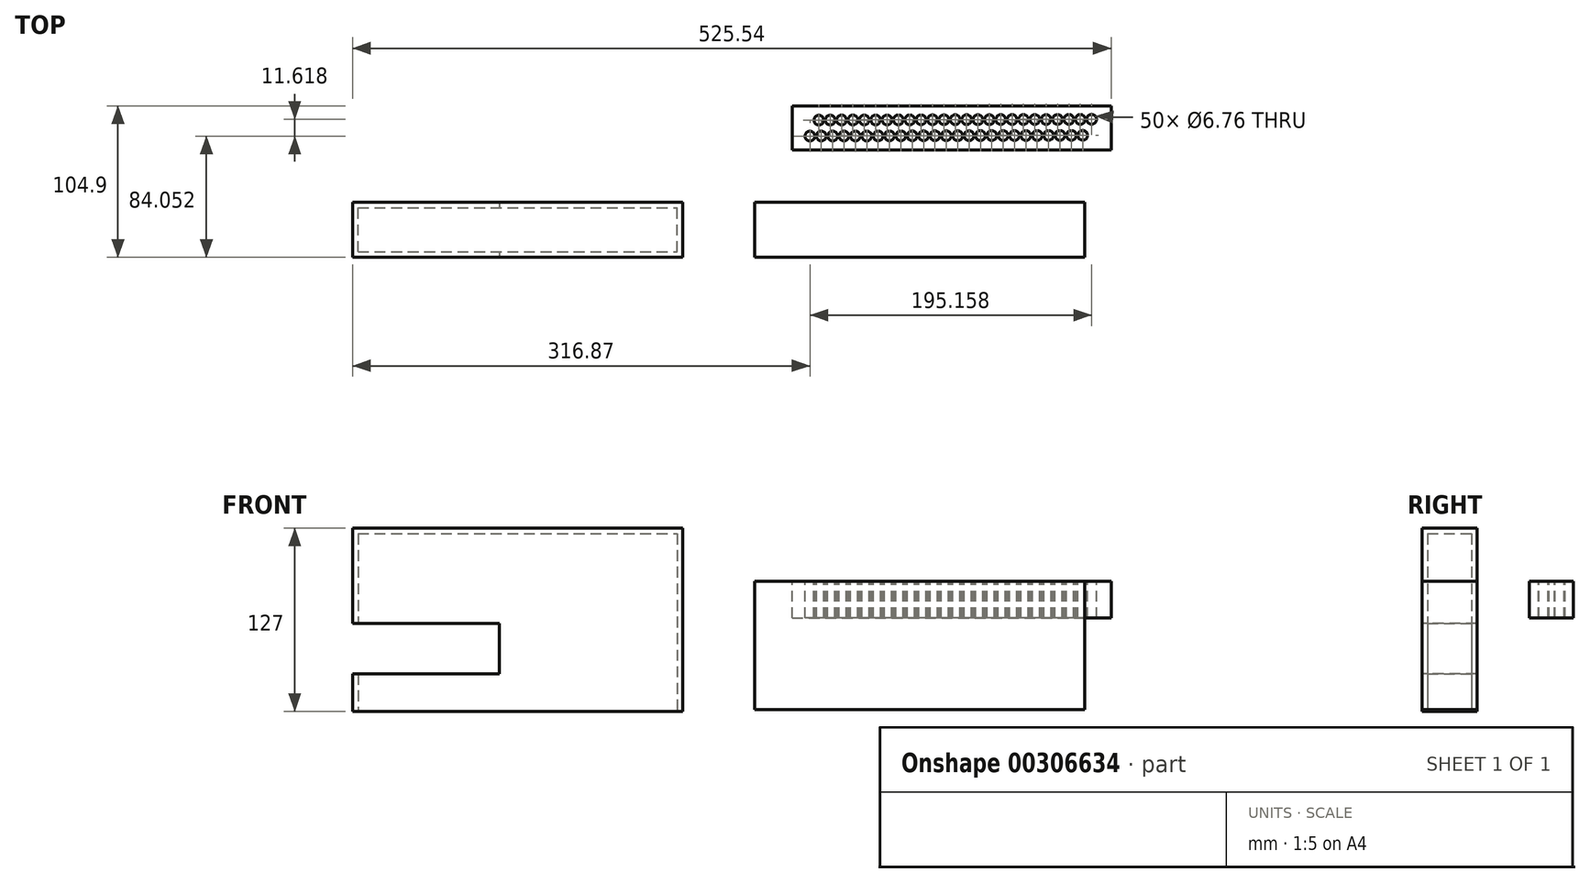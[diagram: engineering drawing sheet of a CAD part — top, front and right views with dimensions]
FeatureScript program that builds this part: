
annotation { "Feature Type Name" : "Feature", "Feature Type Description" : "" }
export const myFeature = defineFeature(function(context is Context, id is Id, definition is map)
    precondition{}
    {
        {
            var Q0;
            Q0=qCreatedBy(makeId("Front.planeOp"),FACE);
            var sketch = newSketch(context, id + "F0", { "sketchPlane" : qUnion([Q0])});
            skLineSegment(sketch, "E0.bottom", {"start": v(-85.07, 109.67) * mm, "end": v(143.53, 109.67) * mm});
            skLineSegment(sketch, "E0.top", {"start": v(-85.07, -17.33) * mm, "end": v(143.53, -17.33) * mm});
            skLineSegment(sketch, "E0.left", {"start": v(-85.07, 109.67) * mm, "end": v(-85.07, -17.33) * mm});
            skLineSegment(sketch, "E0.right", {"start": v(143.53, 109.67) * mm, "end": v(143.53, -17.33) * mm});
            skSolve(sketch);
        }
        {
            var Q0;
            Q0=makeQuery(id+"F0.imprint","IMPRINT",FACE,{"disambiguationData":[TD([[makeQuery(id+"F0.imprint","IMPRINT",EDGE,{"derivedFrom":sQuery(id+"F0.wireOp",EDGE,"E0.bottom")}),-1.0]])]});
            extrude(context, id + "F1", {"entities" : qUnion([Q0]), "depth" : 38.1 * mm});
        }
        {
            var Q0;
            Q0=makeQuery(id+"F1.opExtrude","SWEPT_FACE",FACE,{"disambiguationData":[OSD([sQuery(id+"F0.wireOp",EDGE,"E0.top")])]});
            var Q1;
            Q1=makeQuery(id+"F1.opExtrude","SWEPT_BODY",BODY,{"disambiguationData":[OSD([sQuery(id+"F0.wireOp",EDGE,"E0.bottom"),sQuery(id+"F0.wireOp",EDGE,"E0.top"),sQuery(id+"F0.wireOp",EDGE,"E0.left"),sQuery(id+"F0.wireOp",EDGE,"E0.right")])]});
            shell(context, id + "F2", {"entities" : qUnion([Q0]), "parts" : qUnion([Q1]), "thickness" : 3.8 * mm});
        }
        {
            var Q0;
            Q0=makeQuery(id+"F1.opExtrude","SWEPT_FACE",FACE,{"disambiguationData":[OSD([sQuery(id+"F0.wireOp",EDGE,"E0.left")])]});
            var sketch = newSketch(context, id + "F3", { "sketchPlane" : qUnion([Q0])});
            skLineSegment(sketch, "E1.bottom", {"start": v(0, 43.72) * mm, "end": v(38.1, 43.72) * mm});
            skLineSegment(sketch, "E1.top", {"start": v(0, 8.72) * mm, "end": v(38.1, 8.72) * mm});
            skLineSegment(sketch, "E1.left", {"start": v(0, 43.72) * mm, "end": v(0, 8.72) * mm});
            skLineSegment(sketch, "E1.right", {"start": v(38.1, 43.72) * mm, "end": v(38.1, 8.72) * mm});
            skSolve(sketch);
        }
        {
            var Q0;
            Q0=makeQuery(id+"F3.imprint","IMPRINT",FACE,{"disambiguationData":[TD([[makeQuery(id+"F3.imprint","IMPRINT",EDGE,{"derivedFrom":sQuery(id+"F3.wireOp",EDGE,"E1.bottom")}),-1.0]])]});
            extrude(context, id + "F4", {"entities" : qUnion([Q0]), "operationType" : NewBodyOperationType.REMOVE, "oppositeDirection" : true, "depth" : 101.6 * mm});
        }
        {
            var Q0;
            Q0=qCreatedBy(makeId("Front.planeOp"),FACE);
            var sketch = newSketch(context, id + "F5", { "sketchPlane" : qUnion([Q0])});
            skLineSegment(sketch, "E2.bottom", {"start": v(193.6, 72.7) * mm, "end": v(422.2, 72.7) * mm});
            skLineSegment(sketch, "E2.top", {"start": v(193.6, -16.2) * mm, "end": v(422.2, -16.2) * mm});
            skLineSegment(sketch, "E2.left", {"start": v(193.6, 72.7) * mm, "end": v(193.6, -16.2) * mm});
            skLineSegment(sketch, "E2.right", {"start": v(422.2, 72.7) * mm, "end": v(422.2, -16.2) * mm});
            skSolve(sketch);
        }
        {
            var Q0;
            Q0=makeQuery(id+"F5.imprint","IMPRINT",FACE,{"disambiguationData":[TD([[makeQuery(id+"F5.imprint","IMPRINT",EDGE,{"derivedFrom":sQuery(id+"F5.wireOp",EDGE,"E2.bottom")}),-1.0]])]});
            extrude(context, id + "F6", {"entities" : qUnion([Q0]), "depth" : 38.1 * mm});
        }
        {
            var Q0;
            Q0=makeQuery(id+"F6.opExtrude","SWEPT_FACE",FACE,{"disambiguationData":[OSD([sQuery(id+"F5.wireOp",EDGE,"E2.bottom")])]});
            var sketch = newSketch(context, id + "F7", { "sketchPlane" : qUnion([Q0])});
            skLineSegment(sketch, "E3.bottom", {"start": v(219.5, 66.8) * mm, "end": v(440.47, 66.8) * mm});
            skLineSegment(sketch, "E3.top", {"start": v(219.5, 36.32) * mm, "end": v(440.47, 36.32) * mm});
            skLineSegment(sketch, "E3.left", {"start": v(219.5, 66.8) * mm, "end": v(219.5, 36.32) * mm});
            skLineSegment(sketch, "E3.right", {"start": v(440.47, 66.8) * mm, "end": v(440.47, 36.32) * mm});
            skPoint(sketch, "E4", {"position": v(231.8, 45.95) * mm});
            skPoint(sketch, "E5.0.1.0", {"position": v(237.98, 57.05) * mm});
            skPoint(sketch, "E5.1.0.0", {"position": v(239.67, 45.97) * mm});
            skPoint(sketch, "E5.1.1.0", {"position": v(245.86, 57.07) * mm});
            skPoint(sketch, "E5.2.0.0", {"position": v(247.55, 46) * mm});
            skPoint(sketch, "E5.2.1.0", {"position": v(253.73, 57.09) * mm});
            skPoint(sketch, "E5.3.0.0", {"position": v(255.42, 46.02) * mm});
            skPoint(sketch, "E5.3.1.0", {"position": v(261.6, 57.11) * mm});
            skPoint(sketch, "E5.4.0.0", {"position": v(263.3, 46.04) * mm});
            skPoint(sketch, "E5.4.1.0", {"position": v(269.48, 57.13) * mm});
            skPoint(sketch, "E5.5.0.0", {"position": v(271.17, 46.06) * mm});
            skPoint(sketch, "E5.5.1.0", {"position": v(277.35, 57.15) * mm});
            skPoint(sketch, "E5.6.0.0", {"position": v(279.04, 46.08) * mm});
            skPoint(sketch, "E5.6.1.0", {"position": v(285.23, 57.18) * mm});
            skPoint(sketch, "E5.7.0.0", {"position": v(286.92, 46.1) * mm});
            skPoint(sketch, "E5.7.1.0", {"position": v(293.1, 57.2) * mm});
            skPoint(sketch, "E5.8.0.0", {"position": v(294.8, 46.13) * mm});
            skPoint(sketch, "E5.8.1.0", {"position": v(300.97, 57.22) * mm});
            skPoint(sketch, "E5.9.0.0", {"position": v(302.67, 46.15) * mm});
            skPoint(sketch, "E5.9.1.0", {"position": v(308.85, 57.24) * mm});
            skPoint(sketch, "E5.10.0.0", {"position": v(310.54, 46.17) * mm});
            skPoint(sketch, "E5.10.1.0", {"position": v(316.72, 57.26) * mm});
            skPoint(sketch, "E5.11.0.0", {"position": v(318.41, 46.2) * mm});
            skPoint(sketch, "E5.11.1.0", {"position": v(324.6, 57.29) * mm});
            skPoint(sketch, "E5.12.0.0", {"position": v(326.29, 46.21) * mm});
            skPoint(sketch, "E5.12.1.0", {"position": v(332.47, 57.3) * mm});
            skPoint(sketch, "E5.13.0.0", {"position": v(334.16, 46.24) * mm});
            skPoint(sketch, "E5.13.1.0", {"position": v(340.34, 57.33) * mm});
            skPoint(sketch, "E5.14.0.0", {"position": v(342.04, 46.26) * mm});
            skPoint(sketch, "E5.14.1.0", {"position": v(348.22, 57.35) * mm});
            skPoint(sketch, "E5.15.0.0", {"position": v(349.9, 46.28) * mm});
            skPoint(sketch, "E5.15.1.0", {"position": v(356.1, 57.37) * mm});
            skPoint(sketch, "E5.16.0.0", {"position": v(357.78, 46.3) * mm});
            skPoint(sketch, "E5.16.1.0", {"position": v(363.97, 57.4) * mm});
            skPoint(sketch, "E5.17.0.0", {"position": v(365.66, 46.32) * mm});
            skPoint(sketch, "E5.17.1.0", {"position": v(371.84, 57.42) * mm});
            skPoint(sketch, "E5.18.0.0", {"position": v(373.53, 46.35) * mm});
            skPoint(sketch, "E5.18.1.0", {"position": v(379.71, 57.44) * mm});
            skPoint(sketch, "E5.19.0.0", {"position": v(381.4, 46.37) * mm});
            skPoint(sketch, "E5.19.1.0", {"position": v(387.59, 57.46) * mm});
            skPoint(sketch, "E5.20.0.0", {"position": v(389.28, 46.39) * mm});
            skPoint(sketch, "E5.20.1.0", {"position": v(395.46, 57.48) * mm});
            skPoint(sketch, "E5.21.0.0", {"position": v(397.15, 46.41) * mm});
            skPoint(sketch, "E5.21.1.0", {"position": v(403.34, 57.5) * mm});
            skPoint(sketch, "E5.22.0.0", {"position": v(405.03, 46.43) * mm});
            skPoint(sketch, "E5.22.1.0", {"position": v(411.2, 57.53) * mm});
            skPoint(sketch, "E5.23.0.0", {"position": v(412.9, 46.45) * mm});
            skPoint(sketch, "E5.23.1.0", {"position": v(419.08, 57.55) * mm});
            skPoint(sketch, "E5.24.0.0", {"position": v(420.77, 46.48) * mm});
            skPoint(sketch, "E5.24.1.0", {"position": v(426.96, 57.57) * mm});
            skLineSegment(sketch, "E5.direction1", {"start": v(231.8, 45.95) * mm, "end": v(239.67, 45.97) * mm, "construction": true});
            skLineSegment(sketch, "E5.direction2", {"start": v(231.8, 45.95) * mm, "end": v(237.98, 57.05) * mm, "construction": true});
            skSolve(sketch);
        }
        {
            var Q0;
            Q0=makeQuery(id+"F7.imprint","IMPRINT",FACE,{"disambiguationData":[TD([[makeQuery(id+"F7.imprint","IMPRINT",EDGE,{"derivedFrom":sQuery(id+"F7.wireOp",EDGE,"E3.bottom")}),-1.0]])]});
            extrude(context, id + "F8", {"entities" : qUnion([Q0]), "oppositeDirection" : true, "depth" : 25.4 * mm});
        }
        {
            var Q0;
            Q0=sQuery(id+"F7.wireOp",VERTEX,"E4");
            var Q1;
            Q1=sQuery(id+"F7.wireOp",VERTEX,"E5.1.0.0");
            var Q2;
            Q2=sQuery(id+"F7.wireOp",VERTEX,"E5.2.0.0");
            var Q3;
            Q3=sQuery(id+"F7.wireOp",VERTEX,"E5.3.0.0");
            var Q4;
            Q4=sQuery(id+"F7.wireOp",VERTEX,"E5.4.0.0");
            var Q5;
            Q5=sQuery(id+"F7.wireOp",VERTEX,"E5.5.0.0");
            var Q6;
            Q6=sQuery(id+"F7.wireOp",VERTEX,"E5.7.0.0");
            var Q7;
            Q7=sQuery(id+"F7.wireOp",VERTEX,"E5.6.0.0");
            var Q8;
            Q8=sQuery(id+"F7.wireOp",VERTEX,"E5.8.0.0");
            var Q9;
            Q9=sQuery(id+"F7.wireOp",VERTEX,"E5.9.0.0");
            var Q10;
            Q10=sQuery(id+"F7.wireOp",VERTEX,"E5.10.0.0");
            var Q11;
            Q11=sQuery(id+"F7.wireOp",VERTEX,"E5.11.0.0");
            var Q12;
            Q12=sQuery(id+"F7.wireOp",VERTEX,"E5.12.0.0");
            var Q13;
            Q13=sQuery(id+"F7.wireOp",VERTEX,"E5.14.0.0");
            var Q14;
            Q14=sQuery(id+"F7.wireOp",VERTEX,"E5.13.0.0");
            var Q15;
            Q15=sQuery(id+"F7.wireOp",VERTEX,"E5.15.0.0");
            var Q16;
            Q16=sQuery(id+"F7.wireOp",VERTEX,"E5.16.0.0");
            var Q17;
            Q17=sQuery(id+"F7.wireOp",VERTEX,"E5.17.0.0");
            var Q18;
            Q18=sQuery(id+"F7.wireOp",VERTEX,"E5.18.0.0");
            var Q19;
            Q19=sQuery(id+"F7.wireOp",VERTEX,"E5.19.0.0");
            var Q20;
            Q20=sQuery(id+"F7.wireOp",VERTEX,"E5.20.0.0");
            var Q21;
            Q21=sQuery(id+"F7.wireOp",VERTEX,"E5.21.0.0");
            var Q22;
            Q22=sQuery(id+"F7.wireOp",VERTEX,"E5.22.0.0");
            var Q23;
            Q23=sQuery(id+"F7.wireOp",VERTEX,"E5.23.0.0");
            var Q24;
            Q24=sQuery(id+"F7.wireOp",VERTEX,"E5.24.0.0");
            var Q25;
            Q25=sQuery(id+"F7.wireOp",VERTEX,"E5.24.1.0");
            var Q26;
            Q26=sQuery(id+"F7.wireOp",VERTEX,"E5.24.1.0");
            var Q27;
            Q27=sQuery(id+"F7.wireOp",VERTEX,"E5.23.1.0");
            var Q28;
            Q28=sQuery(id+"F7.wireOp",VERTEX,"E5.22.1.0");
            var Q29;
            Q29=sQuery(id+"F7.wireOp",VERTEX,"E5.21.1.0");
            var Q30;
            Q30=sQuery(id+"F7.wireOp",VERTEX,"E5.20.1.0");
            var Q31;
            Q31=sQuery(id+"F7.wireOp",VERTEX,"E5.19.1.0");
            var Q32;
            Q32=sQuery(id+"F7.wireOp",VERTEX,"E5.18.1.0");
            var Q33;
            Q33=sQuery(id+"F7.wireOp",VERTEX,"E5.17.1.0");
            var Q34;
            Q34=sQuery(id+"F7.wireOp",VERTEX,"E5.16.1.0");
            var Q35;
            Q35=sQuery(id+"F7.wireOp",VERTEX,"E5.15.1.0");
            var Q36;
            Q36=sQuery(id+"F7.wireOp",VERTEX,"E5.14.1.0");
            var Q37;
            Q37=sQuery(id+"F7.wireOp",VERTEX,"E5.13.1.0");
            var Q38;
            Q38=sQuery(id+"F7.wireOp",VERTEX,"E5.12.1.0");
            var Q39;
            Q39=sQuery(id+"F7.wireOp",VERTEX,"E5.11.1.0");
            var Q40;
            Q40=sQuery(id+"F7.wireOp",VERTEX,"E5.10.1.0");
            var Q41;
            Q41=sQuery(id+"F7.wireOp",VERTEX,"E5.9.1.0");
            var Q42;
            Q42=sQuery(id+"F7.wireOp",VERTEX,"E5.8.1.0");
            var Q43;
            Q43=sQuery(id+"F7.wireOp",VERTEX,"E5.6.1.0");
            var Q44;
            Q44=sQuery(id+"F7.wireOp",VERTEX,"E5.7.1.0");
            var Q45;
            Q45=sQuery(id+"F7.wireOp",VERTEX,"E5.5.1.0");
            var Q46;
            Q46=sQuery(id+"F7.wireOp",VERTEX,"E5.4.1.0");
            var Q47;
            Q47=sQuery(id+"F7.wireOp",VERTEX,"E5.3.1.0");
            var Q48;
            Q48=sQuery(id+"F7.wireOp",VERTEX,"E5.1.1.0");
            var Q49;
            Q49=sQuery(id+"F7.wireOp",VERTEX,"E5.2.1.0");
            var Q50;
            Q50=sQuery(id+"F7.wireOp",VERTEX,"E5.0.1.0");
            var Q51;
            Q51=makeQuery(id+"F8.opExtrude","SWEPT_BODY",BODY,{"disambiguationData":[OSD([sQuery(id+"F7.wireOp",EDGE,"E3.bottom"),sQuery(id+"F7.wireOp",EDGE,"E3.top"),sQuery(id+"F7.wireOp",EDGE,"E3.left"),sQuery(id+"F7.wireOp",EDGE,"E3.right")])]});
            hole(context, id + "F9", {"style" : HoleStyle.SIMPLE, "endStyle" : HoleEndStyle.THROUGH, "standardTappedOrClearance" : lookupTablePath({ "standard" : "ANSI", "fit" : "Normal (ASME)", "size" : "1/4", "type" : "Clearance" }), "standardBlindInLast" : lookupTablePath({ "fit" : "Free", "standard" : "ANSI", "size" : "1/4", "type" : "Clearance" }), "holeDiameter" : 6.76 * mm, "tappedDepth" : 12.7 * mm, "tapClearance" : 3, "locations" : qUnion([Q0, Q1, Q2, Q3, Q4, Q5, Q6, Q7, Q8, Q9, Q10, Q11, Q12, Q13, Q14, Q15, Q16, Q17, Q18, Q19, Q20, Q21, Q22, Q23, Q24, Q25, Q26, Q27, Q28, Q29, Q30, Q31, Q32, Q33, Q34, Q35, Q36, Q37, Q38, Q39, Q40, Q41, Q42, Q43, Q44, Q45, Q46, Q47, Q48, Q49, Q50]), "scope" : qUnion([Q51])});
        }
    });
